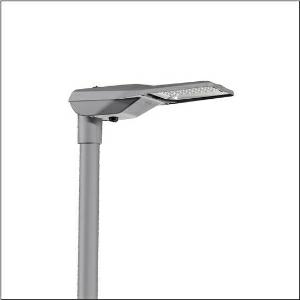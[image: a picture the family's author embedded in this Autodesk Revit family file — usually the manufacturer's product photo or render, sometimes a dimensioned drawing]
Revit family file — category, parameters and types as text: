
# Revit family: streetlight_sl_21_mini___st1_0a_5xe2d63t08hb_d890
name_source: partatom
category: Lighting Fixtures
units: mm (PartAtom-declared; Revit-internal decimal feet)

## family parameters
Cut with Voids When Loaded = No
Host = Face
Light Source = No
Part Type = Normal
Room Calculation Point = No
Round Connector Dimension = Use Diameter
Shared = No

## types (1)
- --- (1 x LED, 8110 lm, 66 W, 2700K)
    Apparent Load = 66 VA
    CIE Flux Codes = 37 72 97 100 100
    Color Rendering = 70
    Color Temperature = 2700K
    Default Elevation = 1800 mm
    Description = Streetlight SL 21 mini, mast luminaire, primary light control with lens, of PMMA, primary optical cover: cover, of toughened safety glass, transparent, light distribution: ST1.0a, light emission: direct distribution, primary light characteristic: asymmetric, installation type: side-entry, post-top, LED, High Power LED, rated luminous flux: 8.110lm, luminous efficacy: 123lm/W, light colour: 727, colour temperature: 2700K, control gear: D4i, control: overheat protection, constant luminous flux control, time-dependent luminous flux control, flexible luminous flux parameterisation, pre-setting: logarithmic dimming characteristic, mains connection: 220..240V, AC, 50/60Hz, start of lifetime: 66W, end of service life: 69W, reduction: 30W, luminaire housing, of diecast aluminium, powder-coated, Siteco® metallic grey (DB 702S), corrosivity category C5 mid according to DIN EN ISO 12944, please order mast flange separately, inclination adjustable: 0°, 5°, 10°, 15°, sealing non-destructively replaceable, multi-level sealing system, length: 628mm, width: 235mm, height: 110mm, mast flange for spigot size: 42mm (side-entry): 5XC10008XM4, 60/48mm (side-entry/post-top): 5XC10108XM2, 76/60mm (side-entry/post-top): 5XC10108XM1, mounting height: 4..8m, Smart Interface below and above, protection rating (complete): IP66, insulation class (complete): insulation class II (safety insulation), certification: CE, ENEC, ENEC+, VDE, impact resistance: IK10, permissible operating ambient temperature for outdoor applications: -40..+50°C, standard-compliant lighting for roads and squares, packaging unit: 1 piece

Light Distribution: ST1.0a
    Height = 110 mm
    Lamp = 1 x LED
    Lamp Light Flux = 8110 lm
    Lamp Power = 66 W
    Lamp count = 1
    Length = 625 mm
    Luminous efficacy = 123 lm/W
    Manufacturer = Siteco
    ModVariant = No
    Model = 5XE2D63T08HB
    Number of Poles = 1
    OnlyDefault = Yes
    Power Factor = 1
    Product Name = Streetlight SL 21 mini | ST1.0a
    Product group = mast luminaire | pylon top
    ProductGroupID = 6100
    Protection Class = Protection class II
    Protection Degree = IP 66
    RLX_Detail_Level = 1
    RLX_Emergency_Light_Flux = 0 lm
    RLX_Emergency_Type = 0
    RLX_Emergency_Type_DB = No
    RlxData = <blob elided: 26241 chars, md5=6adf44df>
    Socket = socket
    Standby Power = 0 W
    System Light Flux = 8110 lm
    System Power = 66 W
    Type Comments = factory setting: luminous flux: 100 % | dim-lin: 254 | 670 mA
    Type Image = l_1003514.jpg
    URL = http://relux.com
    VarID = @adj_188398
    Voltage = 0 V
    Weight = 0.00 kg
    Width = 234 mm

## geometry (parser evidence)
native form markers: Blend x4, Sweep x9
no freeform markers — native parametric forms only
